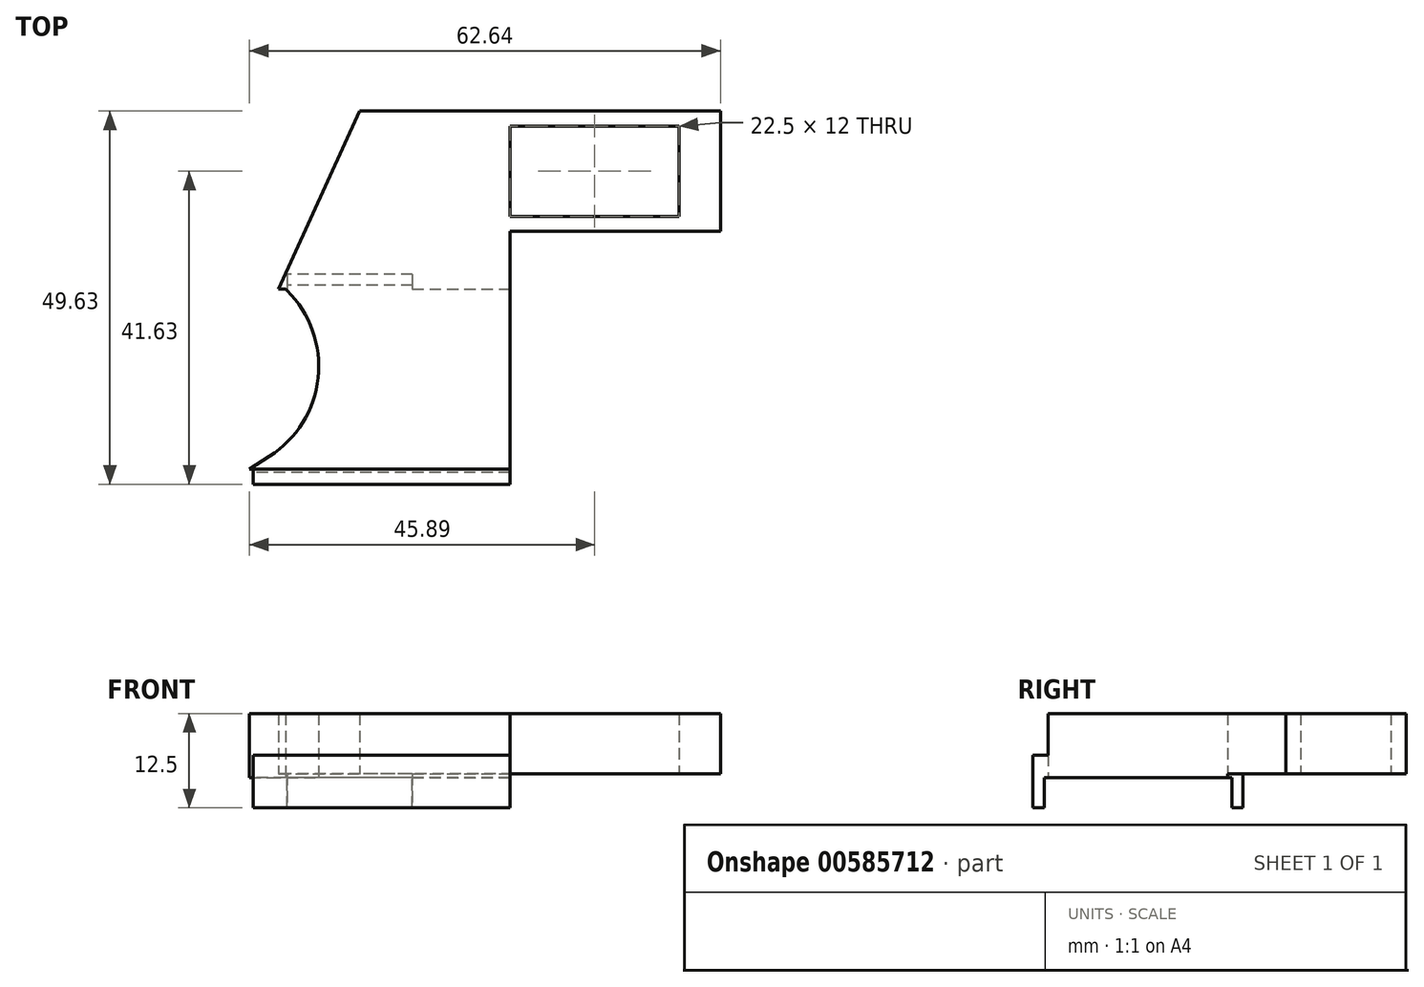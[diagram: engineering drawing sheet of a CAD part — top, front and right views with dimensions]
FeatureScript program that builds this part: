
annotation { "Feature Type Name" : "Feature", "Feature Type Description" : "" }
export const myFeature = defineFeature(function(context is Context, id is Id, definition is map)
    precondition{}
    {
        {
            var Q0;
            Q0=qCreatedBy(makeId("Top.planeOp"),FACE);
            var sketch = newSketch(context, id + "F0", { "sketchPlane" : qUnion([Q0])});
            skLineSegment(sketch, "E0", {"start": v(-54.8, -60.73) * mm, "end": v(43.9, -60.73) * mm});
            skLineSegment(sketch, "E1.MirrorCS", {"start": v(-17, -132.44) * mm, "end": v(-16.91, -132.24) * mm, "construction": true});
            skLineSegment(sketch, "E2.MirrorCS", {"start": v(-16.91, -132.24) * mm, "end": v(-16.72, -132.08) * mm, "construction": true});
            skLineSegment(sketch, "E3.MirrorCS", {"start": v(-13.77, -132.88) * mm, "end": v(-13.7, -132.44) * mm, "construction": true});
            skLineSegment(sketch, "E4.MirrorCS", {"start": v(-16.72, -132.08) * mm, "end": v(-16.39, -132.06) * mm, "construction": true});
            skLineSegment(sketch, "E5.MirrorCS", {"start": v(-11.91, -134.28) * mm, "end": v(-12.1, -133.88) * mm, "construction": true});
            skLineSegment(sketch, "E6.MirrorCS", {"start": v(-13.7, -132.44) * mm, "end": v(-13.62, -132.24) * mm, "construction": true});
            skLineSegment(sketch, "E7.MirrorCS", {"start": v(-15.77, -132.44) * mm, "end": v(-15.86, -132.24) * mm, "construction": true});
            skLineSegment(sketch, "E8.MirrorCS", {"start": v(-17, -116.08) * mm, "end": v(-16.91, -116.27) * mm, "construction": true});
            skLineSegment(sketch, "E9.MirrorCS", {"start": v(-12.56, -132.24) * mm, "end": v(-12.76, -132.08) * mm, "construction": true});
            skLineSegment(sketch, "E10.MirrorCS", {"start": v(-12.1, -133.88) * mm, "end": v(-12.25, -133.47) * mm, "construction": true});
            skLineSegment(sketch, "E11.MirrorCS", {"start": v(-15.21, -134.28) * mm, "end": v(-15.4, -133.88) * mm, "construction": true});
            skLineSegment(sketch, "E12.MirrorCS", {"start": v(-15.86, -132.24) * mm, "end": v(-16.05, -132.08) * mm, "construction": true});
            skLineSegment(sketch, "E13.MirrorCS", {"start": v(-12.76, -132.08) * mm, "end": v(-13.09, -132.06) * mm, "construction": true});
            skLineSegment(sketch, "E14.MirrorCS", {"start": v(-15.77, -116.08) * mm, "end": v(-15.86, -116.27) * mm, "construction": true});
            skLineSegment(sketch, "E15.MirrorCS", {"start": v(-12.25, -133.47) * mm, "end": v(-12.4, -132.88) * mm, "construction": true});
            skLineSegment(sketch, "E16.MirrorCS", {"start": v(-13.93, -133.47) * mm, "end": v(-13.77, -132.88) * mm, "construction": true});
            skLineSegment(sketch, "E17.MirrorCS", {"start": v(-12.4, -132.88) * mm, "end": v(-12.48, -132.44) * mm, "construction": true});
            skLineSegment(sketch, "E18.MirrorCS", {"start": v(-15.4, -133.88) * mm, "end": v(-15.55, -133.47) * mm, "construction": true});
            skLineSegment(sketch, "E19.MirrorCS", {"start": v(-16.05, -132.08) * mm, "end": v(-16.39, -132.06) * mm, "construction": true});
            skLineSegment(sketch, "E20.MirrorCS", {"start": v(-13.62, -132.24) * mm, "end": v(-13.42, -132.08) * mm, "construction": true});
            skLineSegment(sketch, "E21.MirrorCS", {"start": v(-12.48, -116.08) * mm, "end": v(-12.56, -116.27) * mm, "construction": true});
            skLineSegment(sketch, "E22.MirrorCS", {"start": v(-15.21, -137.27) * mm, "end": v(-15.21, -136.6) * mm});
            skLineSegment(sketch, "E23.MirrorCS", {"start": v(-16.91, -116.27) * mm, "end": v(-16.72, -116.43) * mm, "construction": true});
            skLineSegment(sketch, "E24.MirrorCS", {"start": v(-13.7, -116.08) * mm, "end": v(-13.62, -116.27) * mm, "construction": true});
            skLineSegment(sketch, "E25.MirrorCS", {"start": v(-13.42, -132.08) * mm, "end": v(-13.09, -132.06) * mm, "construction": true});
            skLineSegment(sketch, "E26.MirrorCS", {"start": v(-11.91, -134.28) * mm, "end": v(-10.97, -134.28) * mm, "construction": true});
            skLineSegment(sketch, "E27.MirrorCS", {"start": v(-12.48, -132.44) * mm, "end": v(-12.56, -132.24) * mm, "construction": true});
            skLineSegment(sketch, "E28.MirrorCS", {"start": v(-15.55, -133.47) * mm, "end": v(-15.7, -132.88) * mm, "construction": true});
            skLineSegment(sketch, "E29.MirrorCS", {"start": v(-15.7, -132.88) * mm, "end": v(-15.77, -132.44) * mm, "construction": true});
            skLineSegment(sketch, "E30.MirrorCS", {"start": v(-15.21, -134.28) * mm, "end": v(-14.27, -134.28) * mm, "construction": true});
            skLineSegment(sketch, "E31.MirrorCS", {"start": v(-14.27, -134.28) * mm, "end": v(-14.09, -133.88) * mm, "construction": true});
            skLineSegment(sketch, "E32.MirrorCS", {"start": v(-14.09, -133.88) * mm, "end": v(-13.93, -133.47) * mm, "construction": true});
            skLineSegment(sketch, "E33.MirrorCS", {"start": v(-14.27, -114.24) * mm, "end": v(-14.09, -114.64) * mm, "construction": true});
            skLineSegment(sketch, "E34.MirrorCS", {"start": v(-15.21, -114.24) * mm, "end": v(-14.27, -114.24) * mm, "construction": true});
            skLineSegment(sketch, "E35.MirrorCS", {"start": v(-16.05, -116.43) * mm, "end": v(-16.39, -116.46) * mm, "construction": true});
            skLineSegment(sketch, "E36.MirrorCS", {"start": v(-13.62, -116.27) * mm, "end": v(-13.42, -116.43) * mm, "construction": true});
            skLineSegment(sketch, "E37.MirrorCS", {"start": v(-12.4, -115.64) * mm, "end": v(-12.48, -116.08) * mm, "construction": true});
            skLineSegment(sketch, "E38.MirrorCS", {"start": v(-15.86, -116.27) * mm, "end": v(-16.05, -116.43) * mm, "construction": true});
            skLineSegment(sketch, "E39.MirrorCS", {"start": v(-12.1, -114.64) * mm, "end": v(-12.25, -115.05) * mm, "construction": true});
            skLineSegment(sketch, "E40.MirrorCS", {"start": v(-13.93, -115.05) * mm, "end": v(-13.77, -115.64) * mm, "construction": true});
            skLineSegment(sketch, "E41.MirrorCS", {"start": v(-15.21, -113.34) * mm, "end": v(-15.21, -114.03) * mm});
            skLineSegment(sketch, "E42.MirrorCS", {"start": v(-13.77, -115.64) * mm, "end": v(-13.7, -116.08) * mm, "construction": true});
            skLineSegment(sketch, "E43.MirrorCS", {"start": v(-15.55, -115.05) * mm, "end": v(-15.7, -115.64) * mm, "construction": true});
            skLineSegment(sketch, "E44.MirrorCS", {"start": v(-12.25, -115.05) * mm, "end": v(-12.4, -115.64) * mm, "construction": true});
            skLineSegment(sketch, "E45.MirrorCS", {"start": v(-12.76, -116.43) * mm, "end": v(-13.09, -116.46) * mm, "construction": true});
            skLineSegment(sketch, "E46.MirrorCS", {"start": v(-13.42, -116.43) * mm, "end": v(-13.09, -116.46) * mm, "construction": true});
            skLineSegment(sketch, "E47.MirrorCS", {"start": v(-16.72, -116.43) * mm, "end": v(-16.39, -116.46) * mm, "construction": true});
            skLineSegment(sketch, "E48.MirrorCS", {"start": v(-15.21, -114.24) * mm, "end": v(-15.4, -114.64) * mm, "construction": true});
            skLineSegment(sketch, "E49.MirrorCS", {"start": v(-15.7, -115.64) * mm, "end": v(-15.77, -116.08) * mm, "construction": true});
            skLineSegment(sketch, "E50.MirrorCS", {"start": v(-14.09, -114.64) * mm, "end": v(-13.93, -115.05) * mm, "construction": true});
            skLineSegment(sketch, "E51.MirrorCS", {"start": v(-11.91, -114.24) * mm, "end": v(-12.1, -114.64) * mm, "construction": true});
            skLineSegment(sketch, "E52.MirrorCS", {"start": v(-15.21, -113.34) * mm, "end": v(-15.21, -112.8) * mm});
            skLineSegment(sketch, "E53.MirrorCS", {"start": v(-12.56, -116.27) * mm, "end": v(-12.76, -116.43) * mm, "construction": true});
            skLineSegment(sketch, "E54.MirrorCS", {"start": v(-15.21, -112.8) * mm, "end": v(-15.21, -111.34) * mm});
            skLineSegment(sketch, "E55.MirrorCS", {"start": v(-15.4, -114.64) * mm, "end": v(-15.55, -115.05) * mm, "construction": true});
            skLineSegment(sketch, "E56.MirrorCS", {"start": v(-11.91, -114.24) * mm, "end": v(-10.97, -114.24) * mm, "construction": true});
            skLineSegment(sketch, "E57.MirrorCS", {"start": v(-28.12, -137.27) * mm, "end": v(-28.12, -137.73) * mm});
            skLineSegment(sketch, "E58.MirrorCS", {"start": v(-44.82, -113.54) * mm, "end": v(-45.02, -113.34) * mm});
            skLineSegment(sketch, "E59.MirrorCS", {"start": v(-15.21, -144.96) * mm, "end": v(-15.21, -137.27) * mm});
            skLineSegment(sketch, "E60.MirrorCS", {"start": v(-35.21, -137.27) * mm, "end": v(-28.12, -137.27) * mm});
            skLineSegment(sketch, "E61.MirrorCS", {"start": v(-49.85, -137.27) * mm, "end": v(-47.18, -135.56) * mm});
            skLineSegment(sketch, "E62.MirrorCS", {"start": v(-49.34, -139.28) * mm, "end": v(-49.34, -137.27) * mm});
            skLineSegment(sketch, "E63.MirrorCS", {"start": v(-51.15, -137.27) * mm, "end": v(-47.56, -134.97) * mm});
            skLineSegment(sketch, "E64.MirrorCS", {"start": v(-54.8, -114.03) * mm, "end": v(-54.8, -114.67) * mm});
            skLineSegment(sketch, "E65.MirrorCS", {"start": v(-35.21, -137.27) * mm, "end": v(-15.21, -137.27) * mm});
            skLineSegment(sketch, "E66.MirrorCS", {"start": v(-54.8, -136.6) * mm, "end": v(-54.8, -135.84) * mm});
            skLineSegment(sketch, "E67.MirrorCS", {"start": v(-13.09, -132.06) * mm, "end": v(-13.09, -158.96) * mm, "construction": true});
            skLineSegment(sketch, "E68.MirrorCS", {"start": v(-45.32, -114.03) * mm, "end": v(-46, -113.34) * mm});
            skPoint(sketch, "E69.MirrorP", {"position": v(-49.34, -138.27) * mm});
            skLineSegment(sketch, "E70.MirrorCS", {"start": v(-15.21, -136.6) * mm, "end": v(-15.21, -114.03) * mm});
            skLineSegment(sketch, "E71.MirrorCS", {"start": v(-10.97, -114.24) * mm, "end": v(-10.97, -134.28) * mm, "construction": true});
            skLineSegment(sketch, "E72.MirrorCS", {"start": v(-35.21, -113.34) * mm, "end": v(-15.21, -113.34) * mm});
            skLineSegment(sketch, "E73.MirrorCS", {"start": v(-28.19, -112.8) * mm, "end": v(-44.82, -112.8) * mm});
            skLineSegment(sketch, "E74.MirrorCS", {"start": v(-35.21, -137.27) * mm, "end": v(-51.15, -137.27) * mm});
            skArc(sketch, "E75.MirrorCS", {"start": v(-44.82, -113.54) * mm, "mid": v(-40.72, -125.11) * mm, "end": v(-47.18, -135.56) * mm});
            skLineSegment(sketch, "E76.MirrorCS", {"start": v(-35.21, -113.34) * mm, "end": v(-46, -113.34) * mm});
            skLineSegment(sketch, "E77.MirrorCS", {"start": v(-28.19, -111.34) * mm, "end": v(-44.82, -111.34) * mm});
            skPoint(sketch, "E78.orphan", {"position": v(-45.86, -112.5) * mm});
            skPoint(sketch, "E79.orphan", {"position": v(-54.8, -139.6) * mm});
            skPoint(sketch, "E80.orphan", {"position": v(-54.41, -140.19) * mm});
            skPoint(sketch, "E81.orphan", {"position": v(-54.8, -104.5) * mm});
            skLineSegment(sketch, "E82", {"start": v(-35.21, -113.34) * mm, "end": v(-35.21, -137.27) * mm});
            skLineSegment(sketch, "E83", {"start": v(-35.21, -125.3) * mm, "end": v(-28.64, -125.3) * mm});
            skLineSegment(sketch, "E84.MirrorCS", {"start": v(7.29, -103.65) * mm, "end": v(7.29, -105.65) * mm, "construction": true});
            skLineSegment(sketch, "E85.MirrorCS", {"start": v(12.79, -91.65) * mm, "end": v(12.79, -89.65) * mm});
            skLineSegment(sketch, "E86.MirrorCS", {"start": v(-21.26, -105.65) * mm, "end": v(-15.21, -105.65) * mm});
            skLineSegment(sketch, "E87.MirrorCS", {"start": v(-21.26, -89.65) * mm, "end": v(-21.26, -105.65) * mm});
            skLineSegment(sketch, "E88.MirrorCS", {"start": v(7.29, -105.65) * mm, "end": v(12.79, -105.65) * mm});
            skLineSegment(sketch, "E89.MirrorCS", {"start": v(12.79, -105.65) * mm, "end": v(12.79, -91.65) * mm});
            skLineSegment(sketch, "E90.MirrorCS", {"start": v(-15.21, -91.65) * mm, "end": v(-15.21, -103.65) * mm});
            skLineSegment(sketch, "E91.MirrorCS", {"start": v(12.79, -89.65) * mm, "end": v(-15.21, -89.65) * mm});
            skLineSegment(sketch, "E92.MirrorCS", {"start": v(7.29, -91.65) * mm, "end": v(7.29, -103.65) * mm});
            skLineSegment(sketch, "E93.MirrorCS", {"start": v(-15.21, -91.65) * mm, "end": v(7.29, -91.65) * mm});
            skLineSegment(sketch, "E94.MirrorCS", {"start": v(7.29, -103.65) * mm, "end": v(-15.21, -103.65) * mm});
            skLineSegment(sketch, "E95.MirrorCS", {"start": v(-15.21, -89.65) * mm, "end": v(-21.26, -89.65) * mm});
            skLineSegment(sketch, "E96.MirrorCS", {"start": v(7.29, -105.65) * mm, "end": v(-15.21, -105.65) * mm});
            skLineSegment(sketch, "E97.MirrorCS", {"start": v(-35.21, -89.65) * mm, "end": v(-51.15, -113.34) * mm});
            skLineSegment(sketch, "E98.MirrorCS", {"start": v(-21.26, -89.65) * mm, "end": v(-35.21, -89.65) * mm});
            skLineSegment(sketch, "E99.MirrorCS", {"start": v(-49.34, -111.33) * mm, "end": v(-49.34, -113.34) * mm});
            skLineSegment(sketch, "E100.MirrorCS", {"start": v(-15.21, -105.65) * mm, "end": v(-15.21, -113.34) * mm});
            skLineSegment(sketch, "E101.MirrorCS", {"start": v(-15.21, -139.27) * mm, "end": v(-44.82, -139.27) * mm});
            skLineSegment(sketch, "E102.MirrorCS", {"start": v(-28.12, -137.73) * mm, "end": v(-28.12, -139.28) * mm});
            skLineSegment(sketch, "E103", {"start": v(-44.82, -111.34) * mm, "end": v(-44.82, -112.8) * mm});
            skLineSegment(sketch, "E104", {"start": v(-44.82, -112.8) * mm, "end": v(-44.82, -113.54) * mm});
            skLineSegment(sketch, "E105", {"start": v(-46, -113.34) * mm, "end": v(-35.21, -89.65) * mm});
            skLineSegment(sketch, "E106", {"start": v(-28.19, -111.34) * mm, "end": v(-28.19, -113.34) * mm});
            skLineSegment(sketch, "E107", {"start": v(-44.82, -139.27) * mm, "end": v(-49.34, -139.28) * mm});
            skLineSegment(sketch, "E108", {"start": v(-28.12, -137.73) * mm, "end": v(-15.21, -137.73) * mm});
            skLineSegment(sketch, "E109", {"start": v(-15.21, -137.73) * mm, "end": v(-49.34, -137.73) * mm});
            skSolve(sketch);
        }
        {
            var Q0;
            Q0=makeQuery(id+"F0.imprint","IMPRINT",FACE,{"disambiguationData":[TD([[makeQuery(id+"F0.imprint","IMPRINT",EDGE,{"derivedFrom":sQuery(id+"F0.wireOp",EDGE,"6b123b21-bc53-48c5-9da0-f60a7f1218bb")}),1.0]])]});
            var Q1;
            Q1=makeQuery(id+"F0.imprint","IMPRINT",FACE,{"disambiguationData":[TD([[makeQuery(id+"F0.imprint","IMPRINT",EDGE,{"derivedFrom":sQuery(id+"F0.wireOp",EDGE,"ArCvmxiD-8dGq-m4QV-So7g-3jPKMoKmehT5")}),1.0]])]});
            var Q2;
            Q2=makeQuery(id+"F0.imprint","IMPRINT",FACE,{"disambiguationData":[TD([[makeQuery(id+"F0.imprint","IMPRINT",EDGE,{"derivedFrom":sQuery(id+"F0.wireOp",EDGE,"53408af2-c59a-432b-b7e1-e3d510371c4d")}),-1.0]])]});
            var Q3;
            Q3=makeQuery(id+"F0.imprint","IMPRINT",FACE,{"disambiguationData":[TD([[makeQuery(id+"F0.imprint","IMPRINT",EDGE,{"derivedFrom":sQuery(id+"F0.wireOp",EDGE,"53408af2-c59a-432b-b7e1-e3d510371c4d")}),1.0]])]});
            var Q4;
            {var subQ4=sQuery(id+"F0.wireOp",EDGE,"8f0hC6pL-2LMU-pq2i-KB98-5wFnvLNQmf5m");Q4=makeQuery(id+"F0.imprint","IMPRINT",FACE,{"disambiguationData":[TD([[makeQuery(id+"F0.imprint","IMPRINT",EDGE,{"derivedFrom":subQ4}),1.0]])]});}
            var Q5;
            {var subQ15=sQuery(id+"F0.wireOp",EDGE,"E77.MirrorCS");Q5=makeQuery(id+"F0.imprint","IMPRINT",FACE,{"disambiguationData":[TD([[makeQuery(id+"F0.imprint","IMPRINT",EDGE,{"derivedFrom":subQ15}),-1.0]])]});}
            var Q6;
            {var subQ1=sQuery(id+"F0.wireOp",EDGE,"E22.MirrorCS");Q6=makeQuery(id+"F0.imprint","IMPRINT",FACE,{"disambiguationData":[TD([[makeQuery(id+"F0.imprint","IMPRINT",EDGE,{"derivedFrom":subQ1}),1.0]])]});}
            var Q7;
            {var subQ1=sQuery(id+"F0.wireOp",EDGE,"E61.MirrorCS");Q7=makeQuery(id+"F0.imprint","IMPRINT",FACE,{"disambiguationData":[TD([[makeQuery(id+"F0.imprint","IMPRINT",EDGE,{"derivedFrom":subQ1}),-1.0]])]});}
            var Q8;
            Q8=makeQuery(id+"F0.imprint","IMPRINT",FACE,{"disambiguationData":[TD([[makeQuery(id+"F0.imprint","IMPRINT",EDGE,{"derivedFrom":sQuery(id+"F0.wireOp",EDGE,"E85.MirrorCS")}),1.0]])]});
            var Q9;
            {var subQ5=sQuery(id+"F0.wireOp",EDGE,"E73.MirrorCS");Q9=makeQuery(id+"F0.imprint","IMPRINT",FACE,{"disambiguationData":[TD([[makeQuery(id+"F0.imprint","IMPRINT",EDGE,{"derivedFrom":subQ5}),1.0]])]});}
            var Q10;
            {var subQ0=sQuery(id+"F0.wireOp",EDGE,"E73.MirrorCS");Q10=makeQuery(id+"F0.imprint","IMPRINT",FACE,{"disambiguationData":[TD([[makeQuery(id+"F0.imprint","IMPRINT",EDGE,{"derivedFrom":subQ0}),-1.0]])]});}
            var Q11;
            {var subQ0=sQuery(id+"F0.wireOp",EDGE,"E58.MirrorCS");Q11=makeQuery(id+"F0.imprint","IMPRINT",FACE,{"disambiguationData":[TD([[makeQuery(id+"F0.imprint","IMPRINT",EDGE,{"derivedFrom":subQ0}),-1.0]])]});}
            extrude(context, id + "F1", {"entities" : qUnion([Q0, Q1, Q2, Q3, Q4, Q5, Q6, Q7, Q8, Q9, Q10, Q11]), "depth" : 8.5 * mm, "offsetDistance" : 25 * mm});
        }
        {
            var Q0;
            {var subQ4=sQuery(id+"F0.wireOp",EDGE,"8056081f-cc98-4e2d-a2e0-940295c8c5fa");Q0=makeQuery(id+"F0.imprint","IMPRINT",FACE,{"disambiguationData":[TD([[makeQuery(id+"F0.imprint","IMPRINT",EDGE,{"derivedFrom":subQ4}),-1.0]])]});}
            var Q1;
            Q1=makeQuery(id+"F0.imprint","IMPRINT",FACE,{"disambiguationData":[TD([[makeQuery(id+"F0.imprint","IMPRINT",EDGE,{"derivedFrom":sQuery(id+"F0.wireOp",EDGE,"ueYvpBjH-oOSo-eUJA-NZpD-neCl8LNivI1K")}),-1.0]])]});
            var Q2;
            {var subQ0=sQuery(id+"F0.wireOp",EDGE,"E57.MirrorCS");Q2=makeQuery(id+"F0.imprint","IMPRINT",FACE,{"disambiguationData":[TD([[makeQuery(id+"F0.imprint","IMPRINT",EDGE,{"derivedFrom":subQ0}),-1.0]])]});}
            var Q3;
            {var subQ0=sQuery(id+"F0.wireOp",EDGE,"E107");Q3=makeQuery(id+"F0.imprint","IMPRINT",FACE,{"disambiguationData":[TD([[makeQuery(id+"F0.imprint","IMPRINT",EDGE,{"derivedFrom":subQ0}),-1.0]])]});}
            var Q4;
            {var subQ5=sQuery(id+"F0.wireOp",EDGE,"E57.MirrorCS");Q4=makeQuery(id+"F0.imprint","IMPRINT",FACE,{"disambiguationData":[TD([[makeQuery(id+"F0.imprint","IMPRINT",EDGE,{"derivedFrom":subQ5}),1.0]])]});}
            var Q5;
            {var subQ0=sQuery(id+"F0.wireOp",EDGE,"E101.MirrorCS");var subQ1=sQuery(id+"F0.wireOp",EDGE,"E59.MirrorCS");var subQ2=makeQuery(id+"F0.imprint","INTERSECT",VERTEX,{"derivedFrom":[subQ1,subQ0]});Q5=makeQuery(id+"F0.imprint","IMPRINT",FACE,{"disambiguationData":[TD([[makeQuery(id+"F0.imprint","IMPRINT",EDGE,{"disambiguationData":[TD([[subQ2,-1.0]])],"derivedFrom":subQ1}),1.0]])]});}
            extrude(context, id + "F2", {"entities" : qUnion([Q0, Q1, Q2, Q3, Q4, Q5]), "operationType" : NewBodyOperationType.ADD, "depth" : 3 * mm, "offsetDistance" : 25 * mm});
        }
        {
            var Q0;
            Q0=makeQuery(id+"F0.imprint","IMPRINT",FACE,{"disambiguationData":[TD([[makeQuery(id+"F0.imprint","IMPRINT",EDGE,{"derivedFrom":sQuery(id+"F0.wireOp",EDGE,"ueYvpBjH-oOSo-eUJA-NZpD-neCl8LNivI1K")}),-1.0]])]});
            var Q1;
            {var subQ0=sQuery(id+"F0.wireOp",EDGE,"E107");Q1=makeQuery(id+"F0.imprint","IMPRINT",FACE,{"disambiguationData":[TD([[makeQuery(id+"F0.imprint","IMPRINT",EDGE,{"derivedFrom":subQ0}),-1.0]])]});}
            var Q2;
            {var subQ0=sQuery(id+"F0.wireOp",EDGE,"E101.MirrorCS");var subQ1=sQuery(id+"F0.wireOp",EDGE,"E59.MirrorCS");var subQ2=makeQuery(id+"F0.imprint","INTERSECT",VERTEX,{"derivedFrom":[subQ1,subQ0]});Q2=makeQuery(id+"F0.imprint","IMPRINT",FACE,{"disambiguationData":[TD([[makeQuery(id+"F0.imprint","IMPRINT",EDGE,{"disambiguationData":[TD([[subQ2,-1.0]])],"derivedFrom":subQ1}),1.0]])]});}
            extrude(context, id + "F3", {"entities" : qUnion([Q0, Q1, Q2]), "operationType" : NewBodyOperationType.ADD, "oppositeDirection" : true, "depth" : 4 * mm, "offsetDistance" : 25 * mm});
        }
        {
            var Q0;
            {var subQ0=sQuery(id+"F0.wireOp",EDGE,"53408af2-c59a-432b-b7e1-e3d510371c4d");Q0=makeQuery(id+"F0.imprint","IMPRINT",FACE,{"disambiguationData":[TD([[makeQuery(id+"F0.imprint","IMPRINT",EDGE,{"derivedFrom":subQ0}),1.0]])]});}
            var Q1;
            Q1=makeQuery(id+"F0.imprint","IMPRINT",FACE,{"disambiguationData":[TD([[makeQuery(id+"F0.imprint","IMPRINT",EDGE,{"derivedFrom":sQuery(id+"F0.wireOp",EDGE,"6b123b21-bc53-48c5-9da0-f60a7f1218bb")}),1.0]])]});
            var Q2;
            {var subQ15=sQuery(id+"F0.wireOp",EDGE,"E77.MirrorCS");Q2=makeQuery(id+"F0.imprint","IMPRINT",FACE,{"disambiguationData":[TD([[makeQuery(id+"F0.imprint","IMPRINT",EDGE,{"derivedFrom":subQ15}),-1.0]])]});}
            var Q3;
            Q3=makeQuery(id+"F0.imprint","IMPRINT",FACE,{"disambiguationData":[TD([[makeQuery(id+"F0.imprint","IMPRINT",EDGE,{"derivedFrom":sQuery(id+"F0.wireOp",EDGE,"E85.MirrorCS")}),1.0]])]});
            extrude(context, id + "F4", {"entities" : qUnion([Q0, Q1, Q2, Q3]), "operationType" : NewBodyOperationType.REMOVE, "depth" : .5 * mm, "offsetDistance" : 25 * mm});
        }
        {
            var Q0;
            Q0=makeQuery(id+"F0.imprint","IMPRINT",FACE,{"disambiguationData":[TD([[makeQuery(id+"F0.imprint","IMPRINT",EDGE,{"derivedFrom":sQuery(id+"F0.wireOp",EDGE,"ArCvmxiD-8dGq-m4QV-So7g-3jPKMoKmehT5")}),1.0]])]});
            var Q1;
            {var subQ4=sQuery(id+"F0.wireOp",EDGE,"8f0hC6pL-2LMU-pq2i-KB98-5wFnvLNQmf5m");Q1=makeQuery(id+"F0.imprint","IMPRINT",FACE,{"disambiguationData":[TD([[makeQuery(id+"F0.imprint","IMPRINT",EDGE,{"derivedFrom":subQ4}),1.0]])]});}
            var Q2;
            {var subQ0=sQuery(id+"F0.wireOp",EDGE,"E73.MirrorCS");Q2=makeQuery(id+"F0.imprint","IMPRINT",FACE,{"disambiguationData":[TD([[makeQuery(id+"F0.imprint","IMPRINT",EDGE,{"derivedFrom":subQ0}),-1.0]])]});}
            var Q3;
            {var subQ5=sQuery(id+"F0.wireOp",EDGE,"E73.MirrorCS");Q3=makeQuery(id+"F0.imprint","IMPRINT",FACE,{"disambiguationData":[TD([[makeQuery(id+"F0.imprint","IMPRINT",EDGE,{"derivedFrom":subQ5}),1.0]])]});}
            extrude(context, id + "F5", {"entities" : qUnion([Q0, Q1, Q2, Q3]), "operationType" : NewBodyOperationType.ADD, "depth" : .5 * mm, "offsetDistance" : 25 * mm});
        }
        {
            var Q0;
            Q0=makeQuery(id+"F0.imprint","IMPRINT",FACE,{"disambiguationData":[TD([[makeQuery(id+"F0.imprint","IMPRINT",EDGE,{"derivedFrom":sQuery(id+"F0.wireOp",EDGE,"ArCvmxiD-8dGq-m4QV-So7g-3jPKMoKmehT5")}),1.0]])]});
            var Q1;
            {var subQ0=sQuery(id+"F0.wireOp",EDGE,"E73.MirrorCS");Q1=makeQuery(id+"F0.imprint","IMPRINT",FACE,{"disambiguationData":[TD([[makeQuery(id+"F0.imprint","IMPRINT",EDGE,{"derivedFrom":subQ0}),-1.0]])]});}
            extrude(context, id + "F6", {"entities" : qUnion([Q0, Q1]), "operationType" : NewBodyOperationType.ADD, "oppositeDirection" : true, "depth" : 4 * mm, "offsetDistance" : 25 * mm});
        }
    });
